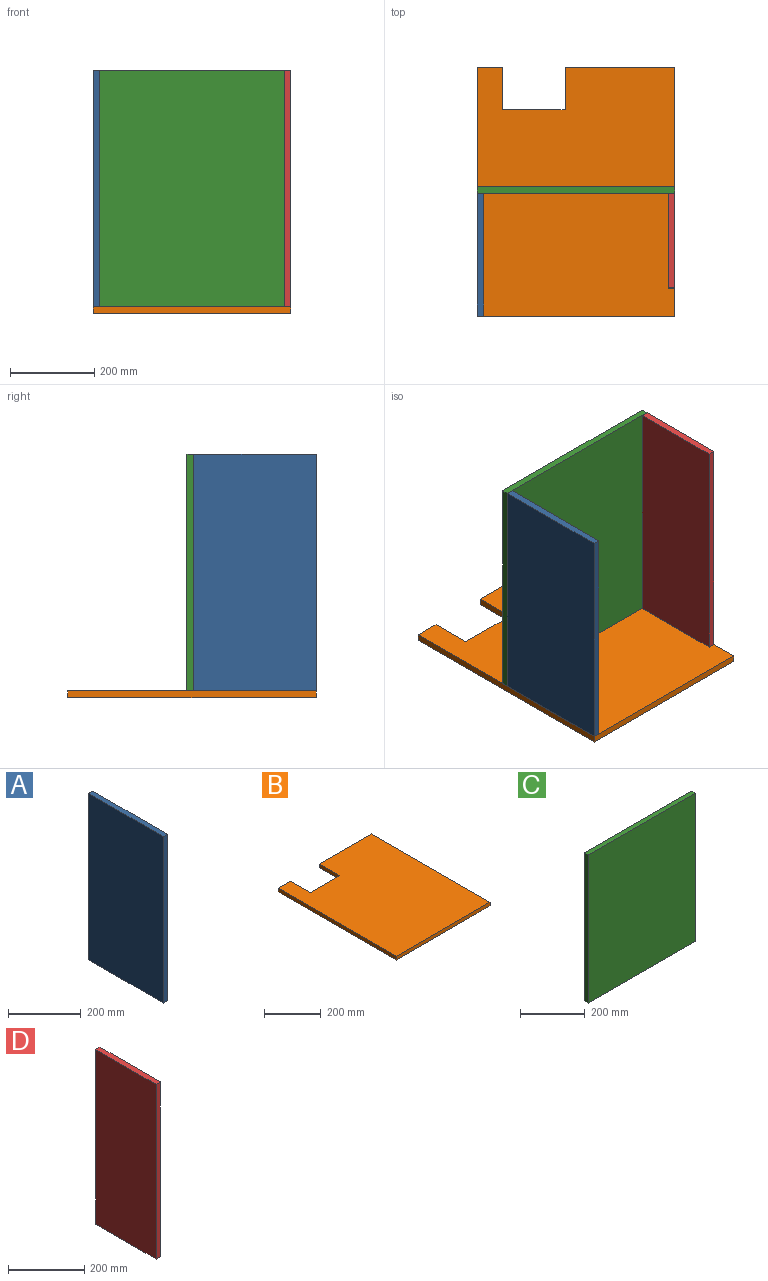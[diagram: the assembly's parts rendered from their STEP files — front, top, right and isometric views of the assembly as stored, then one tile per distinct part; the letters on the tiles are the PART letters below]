
ASSEMBLY  parts=4 mates=3
PART A: 6 faces, bbox 16x291x560 mm
  f0: plane 560x291mm, normal (-1,0,0), area 162960mm2, adj f1,f3,f4,f5
  f1: plane 291x16mm, normal (0,0,-1), area 4656mm2, adj f0,f2,f4,f5
  f2: plane 560x291mm, normal (1,0,0), area 162960mm2, adj f1,f3,f4,f5
  f3: plane 291x16mm, normal (0,0,1), area 4656mm2, adj f0,f2,f4,f5
  f4: plane 560x16mm, normal (0,1,0), area 8960mm2, adj f0,f1,f2,f3
  f5: plane 560x16mm, normal (0,-1,0), area 8960mm2, adj f0,f1,f2,f3
PART B: 10 faces, bbox 468x590x16 mm
  f0: plane 260x16mm, normal (0,1,0), area 4160mm2, adj f3,f5,f6,f9
  f1: plane 590x16mm, normal (-1,0,0), area 9440mm2, adj f2,f4,f5,f6
  f2: plane 468x16mm, normal (0,-1,0), area 7488mm2, adj f1,f3,f5,f6
  f3: plane 590x16mm, normal (1,0,0), area 9440mm2, adj f0,f2,f5,f6
  f4: plane 60x16mm, normal (0,1,0), area 960mm2, adj f1,f5,f6,f7
  f5: plane 590x468mm, normal (0,0,1), area 261320mm2, adj f0,f1,f2,f3,f4,f7,f8,f9
  f6: plane 590x468mm, normal (0,0,-1), area 261320mm2, adj f0,f1,f2,f3,f4,f7,f8,f9
  f7: plane 100x16mm, normal (1,0,0), area 1600mm2, adj f4,f5,f6,f8
  f8: plane 148x16mm, normal (0,1,0), area 2368mm2, adj f5,f6,f7,f9
  f9: plane 100x16mm, normal (-1,0,0), area 1600mm2, adj f0,f5,f6,f8
PART C: 6 faces, bbox 468x16x560 mm
  f0: plane 560x16mm, normal (-1,0,0), area 8960mm2, adj f1,f3,f4,f5
  f1: plane 468x16mm, normal (0,0,-1), area 7488mm2, adj f0,f2,f4,f5
  f2: plane 560x16mm, normal (1,0,0), area 8960mm2, adj f1,f3,f4,f5
  f3: plane 468x16mm, normal (0,0,1), area 7488mm2, adj f0,f2,f4,f5
  f4: plane 560x468mm, normal (0,-1,0), area 262080mm2, adj f0,f1,f2,f3
  f5: plane 560x468mm, normal (0,1,0), area 262080mm2, adj f0,f1,f2,f3
PART D: 6 faces, bbox 16x224x560 mm
  f0: plane 560x224mm, normal (-1,0,0), area 125440mm2, adj f1,f3,f4,f5
  f1: plane 224x16mm, normal (0,0,-1), area 3584mm2, adj f0,f2,f4,f5
  f2: plane 560x224mm, normal (1,0,0), area 125440mm2, adj f1,f3,f4,f5
  f3: plane 224x16mm, normal (0,0,1), area 3584mm2, adj f0,f2,f4,f5
  f4: plane 560x16mm, normal (0,1,0), area 8960mm2, adj f0,f1,f2,f3
  f5: plane 560x16mm, normal (0,-1,0), area 8960mm2, adj f0,f1,f2,f3
PLACE A t=(-11.04,-112.97,35.45)mm
PLACE B t=(-11.04,-112.97,19.45)mm
PLACE C t=(-11.04,194.03,35.45)mm
PLACE D t=(440.96,-45.97,35.45)mm
MATE slider D.f1 <-> B.f5  axis (0,0,-1) through (456.96,-45.97,35.45)mm
MATE slider C.f4 <-> D.f4  axis (0,-1,0) through (456.96,178.03,35.45)mm
MATE slider A.f1 <-> B.f5  axis (0,0,-1) through (-11.04,-112.97,35.45)mm
